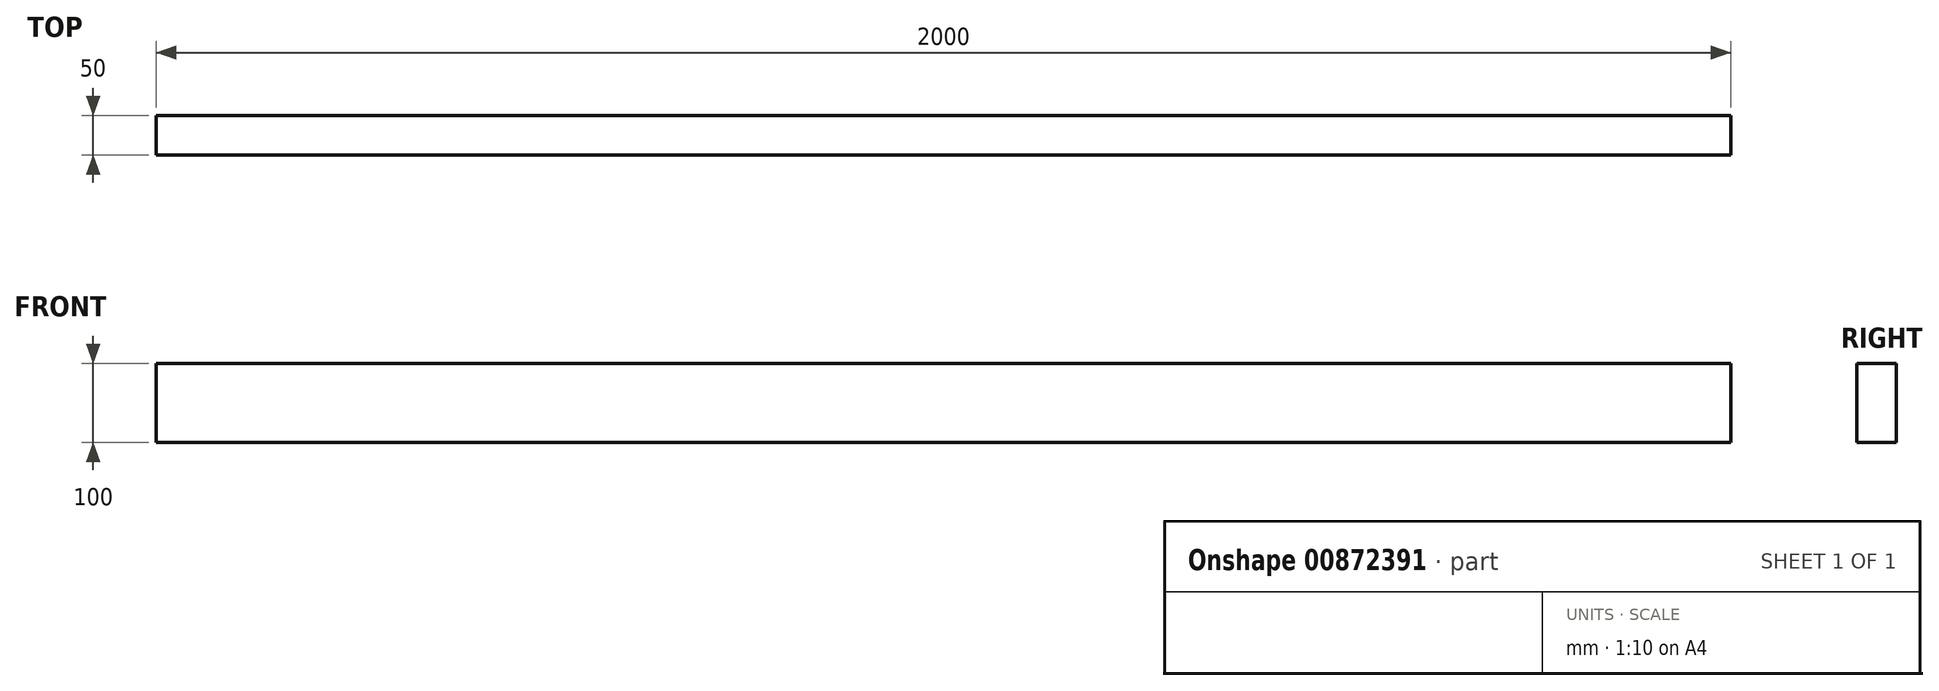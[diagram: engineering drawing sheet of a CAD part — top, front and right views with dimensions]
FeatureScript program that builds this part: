
annotation { "Feature Type Name" : "Feature", "Feature Type Description" : "" }
export const myFeature = defineFeature(function(context is Context, id is Id, definition is map)
    precondition{}
    {
        {
            var Q0;
            Q0=qCreatedBy(makeId("Right.planeOp"),FACE);
            var sketch = newSketch(context, id + "F0", { "sketchPlane" : qUnion([Q0])});
            skLineSegment(sketch, "E0.bottom", {"start": v(-25, 50) * mm, "end": v(25, 50) * mm});
            skLineSegment(sketch, "E0.top", {"start": v(-25, -50) * mm, "end": v(25, -50) * mm});
            skLineSegment(sketch, "E0.left", {"start": v(-25, 50) * mm, "end": v(-25, -50) * mm});
            skLineSegment(sketch, "E0.right", {"start": v(25, 50) * mm, "end": v(25, -50) * mm});
            skSolve(sketch);
        }
        {
            var Q0;
            Q0 = qSketchRegion(id + "F0", true);
            extrude(context, id + "F1", {"entities" : qUnion([Q0]), "depth" : 2000 * mm, "offsetDistance" : 25 * mm});
        }
        {
            var Q0;
            Q0=makeQuery(id+"F1.opExtrude","SWEPT_BODY",BODY,{"disambiguationData":[OSD([sQuery(id+"F0.wireOp",EDGE,"E0.bottom"),sQuery(id+"F0.wireOp",EDGE,"E0.top"),sQuery(id+"F0.wireOp",EDGE,"E0.left"),sQuery(id+"F0.wireOp",EDGE,"E0.right")])]});
            transform(context, id + "F2", {"entities" : qUnion([Q0]), "transformType" : TransformType.TRANSLATION_3D, "dx" : 0 * mm, "dy" : 2000 * mm, "dz" : 0 * mm, "makeCopy" : true});
        }
        {
            var Q0;
            Q0=makeQuery(id+"F1.opExtrude","SWEPT_BODY",BODY,{"disambiguationData":[OSD([sQuery(id+"F0.wireOp",EDGE,"E0.bottom"),sQuery(id+"F0.wireOp",EDGE,"E0.top"),sQuery(id+"F0.wireOp",EDGE,"E0.left"),sQuery(id+"F0.wireOp",EDGE,"E0.right")])]});
            var Q1;
            Q1=makeQuery(id+"F1.opExtrude","CAP_EDGE",EDGE,{"disambiguationData":[OSD([sQuery(id+"F0.wireOp",EDGE,"E0.left")])],"isStart":true});
            transform(context, id + "F3", {"entities" : qUnion([Q0]), "transformType" : TransformType.ROTATION, "transformAxis" : qUnion([Q1]), "angle" : 90 * degree, "oppositeDirection" : true, "makeCopy" : true});
        }
        {
            var Q0;
            Q0=makeQuery(id+"F3.opPattern","COPY",BODY,{"derivedFrom":makeQuery(id+"F1.opExtrude","SWEPT_BODY",BODY,{"disambiguationData":[OSD([sQuery(id+"F0.wireOp",EDGE,"E0.bottom"),sQuery(id+"F0.wireOp",EDGE,"E0.top"),sQuery(id+"F0.wireOp",EDGE,"E0.left"),sQuery(id+"F0.wireOp",EDGE,"E0.right")])]}),"instanceName":"1"});
            deleteBodies(context, id + "F4", {"entities" : qUnion([Q0])});
        }
        {
            var Q0;
            Q0=makeQuery(id+"F1.opExtrude","SWEPT_BODY",BODY,{"disambiguationData":[OSD([sQuery(id+"F0.wireOp",EDGE,"E0.bottom"),sQuery(id+"F0.wireOp",EDGE,"E0.top"),sQuery(id+"F0.wireOp",EDGE,"E0.left"),sQuery(id+"F0.wireOp",EDGE,"E0.right")])]});
            transform(context, id + "F5", {"entities" : qUnion([Q0]), "transformType" : TransformType.TRANSLATION_3D, "dx" : 0 * mm, "dy" : 0 * mm, "dz" : 0 * mm, "makeCopy" : true});
        }
        {
            var Q0;
            Q0=makeQuery(id+"F5.opPattern","COPY",BODY,{"derivedFrom":makeQuery(id+"F1.opExtrude","SWEPT_BODY",BODY,{"disambiguationData":[OSD([sQuery(id+"F0.wireOp",EDGE,"E0.bottom"),sQuery(id+"F0.wireOp",EDGE,"E0.top"),sQuery(id+"F0.wireOp",EDGE,"E0.left"),sQuery(id+"F0.wireOp",EDGE,"E0.right")])]}),"instanceName":"1"});
            deleteBodies(context, id + "F6", {"entities" : qUnion([Q0])});
        }
        {
            var Q0;
            Q0=makeQuery(id+"F2.opPattern","COPY",BODY,{"derivedFrom":makeQuery(id+"F1.opExtrude","SWEPT_BODY",BODY,{"disambiguationData":[OSD([sQuery(id+"F0.wireOp",EDGE,"E0.bottom"),sQuery(id+"F0.wireOp",EDGE,"E0.top"),sQuery(id+"F0.wireOp",EDGE,"E0.left"),sQuery(id+"F0.wireOp",EDGE,"E0.right")])]}),"instanceName":"1"});
            deleteBodies(context, id + "F7", {"entities" : qUnion([Q0])});
        }
    });
